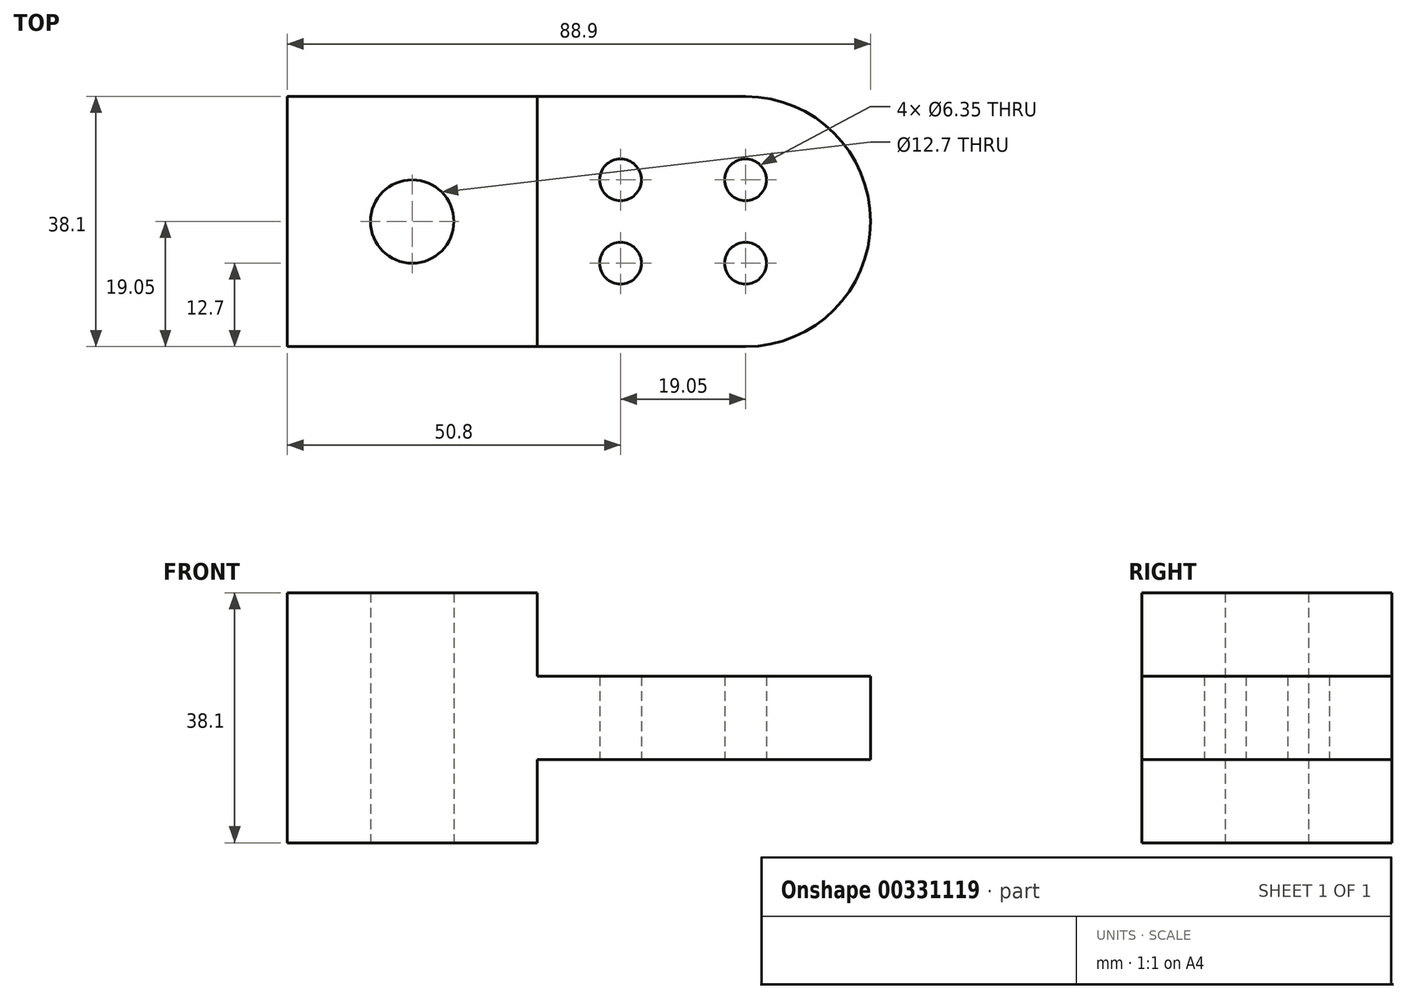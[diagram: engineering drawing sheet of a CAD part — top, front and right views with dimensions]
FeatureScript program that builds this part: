
annotation { "Feature Type Name" : "Feature", "Feature Type Description" : "" }
export const myFeature = defineFeature(function(context is Context, id is Id, definition is map)
    precondition{}
    {
        {
            var Q0;
            Q0=qCreatedBy(makeId("Top.planeOp"),FACE);
            var sketch = newSketch(context, id + "F0", { "sketchPlane" : qUnion([Q0])});
            skLineSegment(sketch, "E0", {"start": v(0, 0) * mm, "end": v(0, 38.1) * mm});
            skLineSegment(sketch, "E1", {"start": v(0, 38.1) * mm, "end": v(38.1, 38.1) * mm});
            skLineSegment(sketch, "E2", {"start": v(38.1, 38.1) * mm, "end": v(38.1, 0) * mm});
            skLineSegment(sketch, "E3", {"start": v(38.1, 0) * mm, "end": v(0, 0) * mm});
            skCircle(sketch, "E4", {"center": v(19.05, 19.05) * mm, "radius": 6.35 * mm});
            skLineSegment(sketch, "E5", {"start": v(38.1, 38.1) * mm, "end": v(69.85, 38.1) * mm});
            skLineSegment(sketch, "E6", {"start": v(38.1, 0) * mm, "end": v(69.85, 0) * mm});
            skArc(sketch, "E7", {"start": v(69.85, 0) * mm, "mid": v(88.9, 19.05) * mm, "end": v(69.85, 38.1) * mm});
            skCircle(sketch, "E8", {"center": v(50.8, 25.4) * mm, "radius": 3.18 * mm});
            skCircle(sketch, "E9", {"center": v(69.85, 25.4) * mm, "radius": 3.18 * mm});
            skCircle(sketch, "E10", {"center": v(69.85, 12.7) * mm, "radius": 3.18 * mm});
            skCircle(sketch, "E11", {"center": v(50.8, 12.7) * mm, "radius": 3.18 * mm});
            skSolve(sketch);
        }
        {
            var Q0;
            Q0 = qSketchRegion(id + "F0", true);
            extrude(context, id + "F1", {"entities" : qUnion([Q0]), "depth" : 12.7 * mm});
        }
        {
            var Q0;
            Q0=makeQuery(id+"F1.opExtrude","CAP_FACE",FACE,{"disambiguationData":[OSD([sQuery(id+"F0.wireOp",EDGE,"E0"),sQuery(id+"F0.wireOp",EDGE,"E1"),sQuery(id+"F0.wireOp",EDGE,"E3"),sQuery(id+"F0.wireOp",EDGE,"E4"),sQuery(id+"F0.wireOp",EDGE,"E5"),sQuery(id+"F0.wireOp",EDGE,"E6"),sQuery(id+"F0.wireOp",EDGE,"E7"),sQuery(id+"F0.wireOp",EDGE,"E8"),sQuery(id+"F0.wireOp",EDGE,"E9"),sQuery(id+"F0.wireOp",EDGE,"E10"),sQuery(id+"F0.wireOp",EDGE,"E11")])],"isStart":false});
            var sketch = newSketch(context, id + "F2", { "sketchPlane" : qUnion([Q0])});
            skLineSegment(sketch, "E12", {"start": v(0, 38.1) * mm, "end": v(38.1, 38.1) * mm});
            skLineSegment(sketch, "E13", {"start": v(38.1, 38.1) * mm, "end": v(38.1, 0) * mm});
            skLineSegment(sketch, "E14", {"start": v(38.1, 0) * mm, "end": v(0, 0) * mm});
            skLineSegment(sketch, "E15", {"start": v(0, 0) * mm, "end": v(0, 38.1) * mm});
            skCircle(sketch, "E16", {"center": v(19.05, 19.05) * mm, "radius": 6.35 * mm});
            skSolve(sketch);
        }
        {
            var Q0;
            Q0 = qSketchRegion(id + "F2", true);
            extrude(context, id + "F3", {"entities" : qUnion([Q0]), "operationType" : NewBodyOperationType.ADD, "depth" : 12.7 * mm, "hasSecondDirection" : true, "secondDirectionOppositeDirection" : true, "secondDirectionDepth" : 25.4 * mm});
        }
    });
